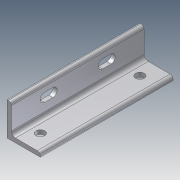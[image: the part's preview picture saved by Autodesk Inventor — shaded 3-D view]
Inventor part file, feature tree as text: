
AUTODESK INVENTOR PART (.ipt)
format: ipt  version: 2012 (Build 160160000, 160)  size: 126,464 bytes
history: native  units: in
note: dims shown in document units (in); Inventor stores cm internally (conversion verified against a paired STEP export)
features: extrude x2, fillet x2, sketch x2, hole x1, pattern_linear x1
ambient origin geometry x8: Origin, YZ Plane, XZ Plane, XY Plane, X Axis, Y Axis, Z Axis, Center Point
bodies: Solid1 (feature_tree)
feature tree (8):
  extrude  "Extrusion1"  Depth=1.0in
  fillet  "Fillet1"  Radius=0.125in
  hole  "Hole1"  [1 undecoded]
  pattern_linear  "Rectangular Pattern1"  Spacing1=0.125in  [1 undecoded]
  fillet  "Fillet3"  Radius=0.7874in
  extrude  "Extrusion2"  Depth=0.094in
  sketch  "Sketch1"  dims[d0=1.0in d1=1.0in d2=0.125in]
  sketch  "Sketch2"  dims[d3=0.125in d4=4.0in d5=0.0in d6=0.125in d7=0.5in d8=0.5in d9=0.265in d10=0.75in d11=0.375in d12=0.25in d13=0.5635in d14=1.0in d15=0.8108in d16=0.7874in d18=3.0in d20=0.094in d21=0.265in d22=0.25in d23=0.25in d24=0.625in d25=0.625in d26=1.0in d27=1.0in d28=1.0in d29=0.0in]
note: 2 required parameter values undecoded (feature->parameter linkage not recoverable at this tier; creation-order binding heuristic only, values carry confidence <= 0.55)
